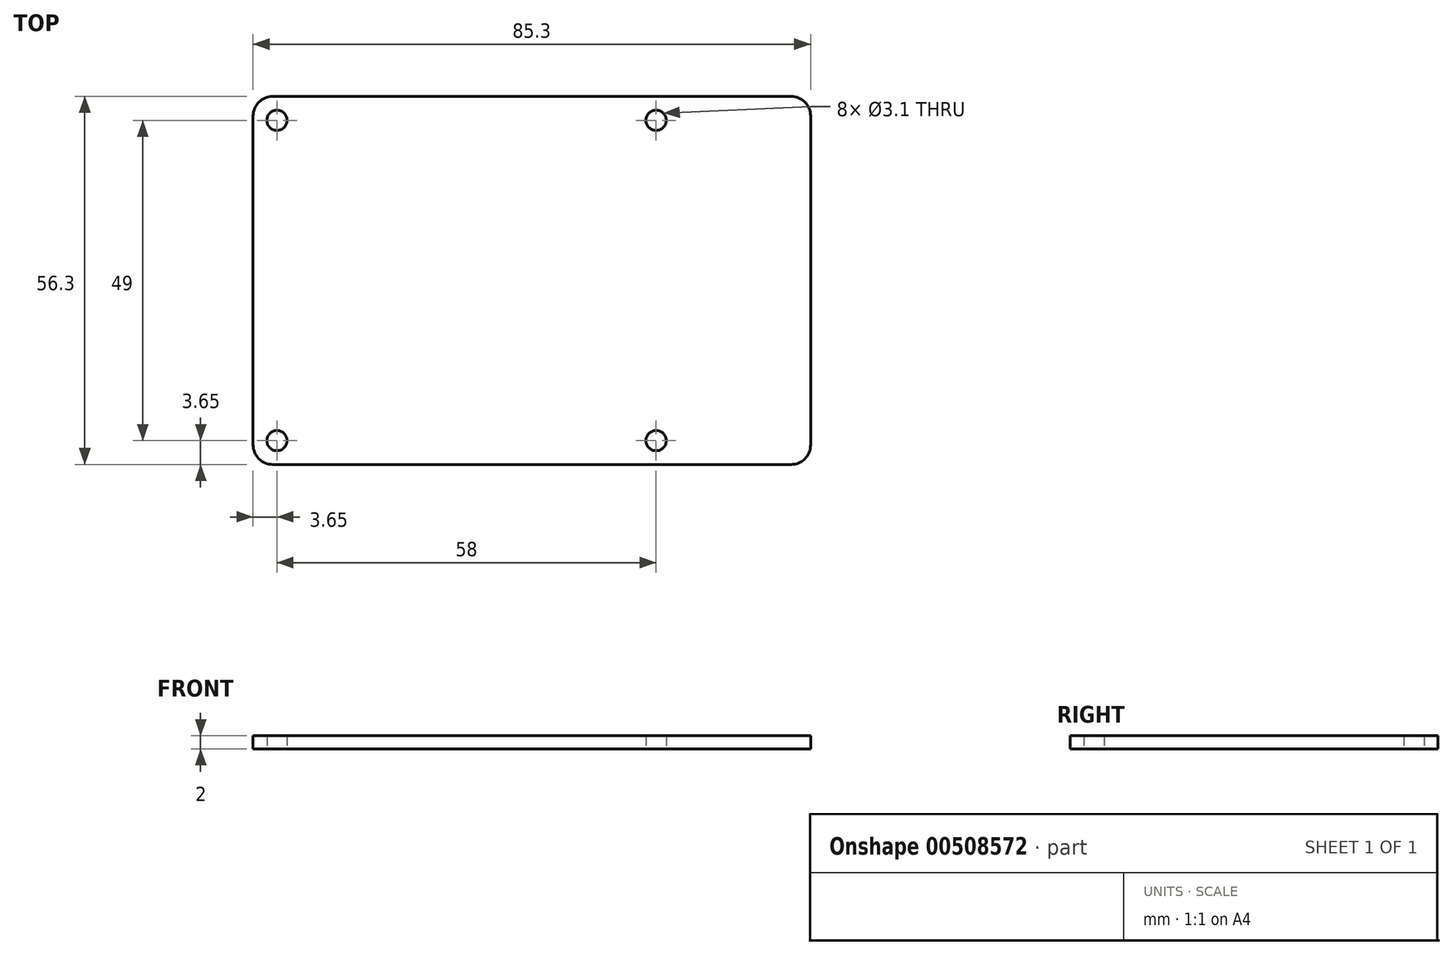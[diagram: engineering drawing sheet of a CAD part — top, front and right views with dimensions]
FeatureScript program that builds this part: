
annotation { "Feature Type Name" : "Feature", "Feature Type Description" : "" }
export const myFeature = defineFeature(function(context is Context, id is Id, definition is map)
    precondition{}
    {
        {
            var Q0;
            Q0=qCreatedBy(makeId("Top.planeOp"),FACE);
            var sketch = newSketch(context, id + "F0", { "sketchPlane" : qUnion([Q0])});
            skLineSegment(sketch, "E0.bottom", {"start": v(42.65, -28.15) * mm, "end": v(-42.65, -28.15) * mm});
            skLineSegment(sketch, "E0.top", {"start": v(42.65, 28.15) * mm, "end": v(-42.65, 28.15) * mm});
            skLineSegment(sketch, "E0.left", {"start": v(42.65, -28.15) * mm, "end": v(42.65, 28.15) * mm});
            skLineSegment(sketch, "E0.right", {"start": v(-42.65, -28.15) * mm, "end": v(-42.65, 28.15) * mm});
            skPoint(sketch, "E0.middle", {"position": v(0, 0) * mm});
            skLineSegment(sketch, "E1.bottom", {"start": v(19, -24.5) * mm, "end": v(-39, -24.5) * mm, "construction": true});
            skLineSegment(sketch, "E1.top", {"start": v(19, 24.5) * mm, "end": v(-39, 24.5) * mm, "construction": true});
            skLineSegment(sketch, "E1.left", {"start": v(19, -24.5) * mm, "end": v(19, 24.5) * mm, "construction": true});
            skLineSegment(sketch, "E1.right", {"start": v(-39, -24.5) * mm, "end": v(-39, 24.5) * mm, "construction": true});
            skPoint(sketch, "E1.middle", {"position": v(-10, 0) * mm});
            skCircle(sketch, "E2", {"center": v(-39, -24.5) * mm, "radius": 1.55 * mm});
            skCircle(sketch, "E3", {"center": v(-39, 24.5) * mm, "radius": 1.55 * mm});
            skCircle(sketch, "E4", {"center": v(19, 24.5) * mm, "radius": 1.55 * mm});
            skCircle(sketch, "E5", {"center": v(19, -24.5) * mm, "radius": 1.55 * mm});
            skSolve(sketch);
        }
        {
            var Q0;
            Q0 = qSketchRegion(id + "F0", true);
            extrude(context, id + "F1", {"entities" : qUnion([Q0]), "depth" : 2 * mm});
        }
        {
            var Q0;
            Q0=makeQuery(id+"F1.opExtrude","SWEPT_EDGE",EDGE,{"disambiguationData":[OSD([sQuery(id+"F0.wireOp",EDGE,"E0.top"),sQuery(id+"F0.wireOp",EDGE,"E0.right")])]});
            var Q1;
            Q1=makeQuery(id+"F1.opExtrude","SWEPT_EDGE",EDGE,{"disambiguationData":[OSD([sQuery(id+"F0.wireOp",EDGE,"E0.bottom"),sQuery(id+"F0.wireOp",EDGE,"E0.right")])]});
            var Q2;
            Q2=makeQuery(id+"F1.opExtrude","SWEPT_EDGE",EDGE,{"disambiguationData":[OSD([sQuery(id+"F0.wireOp",EDGE,"E0.top"),sQuery(id+"F0.wireOp",EDGE,"E0.left")])]});
            var Q3;
            Q3=makeQuery(id+"F1.opExtrude","SWEPT_EDGE",EDGE,{"disambiguationData":[OSD([sQuery(id+"F0.wireOp",EDGE,"E0.bottom"),sQuery(id+"F0.wireOp",EDGE,"E0.left")])]});
            fillet(context, id + "F2", {"entities" : qUnion([Q0, Q1, Q2, Q3]), "radius" : 3 * mm, "tangentPropagation" : true, "allowEdgeOverflow" : false});
        }
    });
